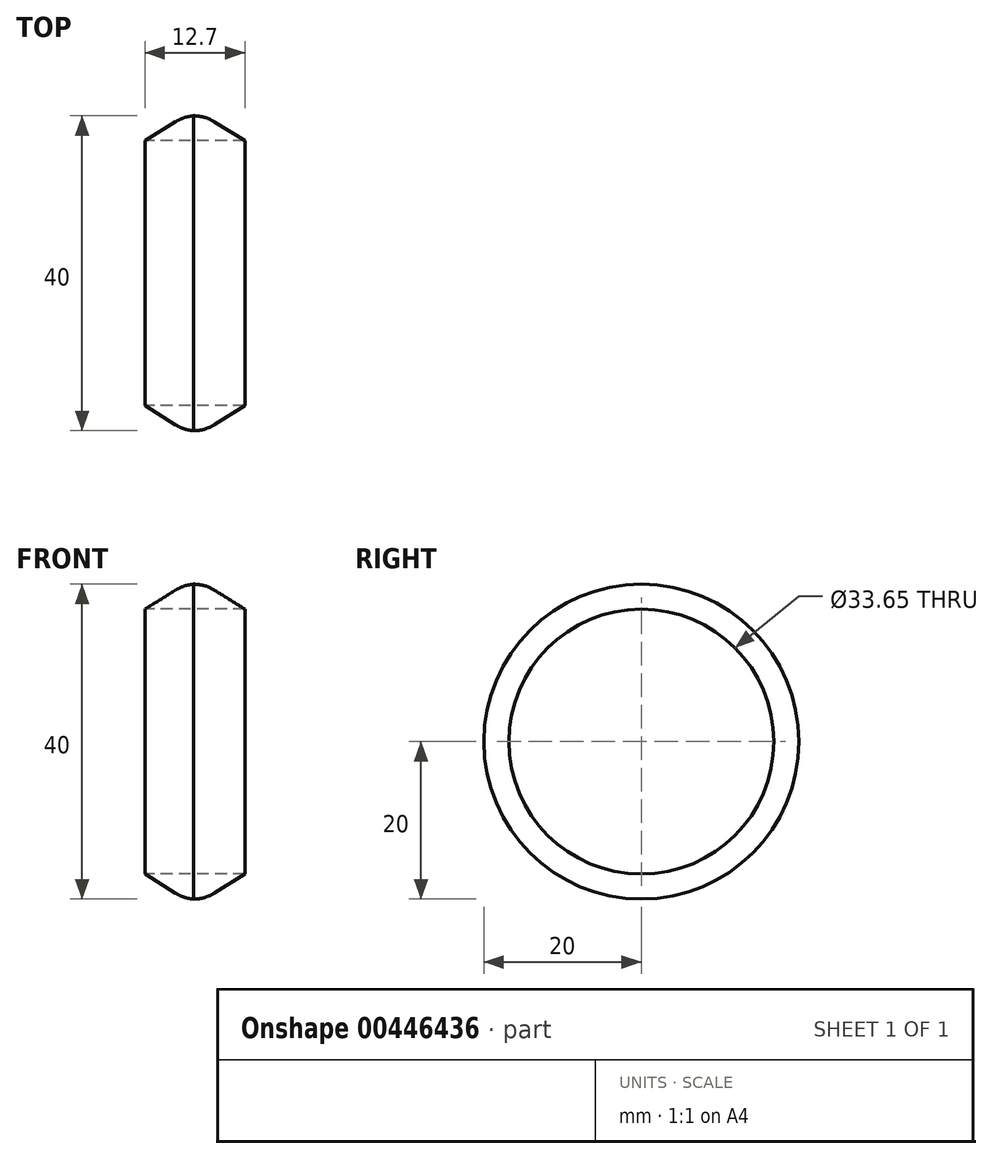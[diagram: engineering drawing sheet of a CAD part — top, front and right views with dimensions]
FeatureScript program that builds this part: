
annotation { "Feature Type Name" : "Feature", "Feature Type Description" : "" }
export const myFeature = defineFeature(function(context is Context, id is Id, definition is map)
    precondition{}
    {
        {
            var Q0;
            Q0=qCreatedBy(makeId("Front.planeOp"),FACE);
            var sketch = newSketch(context, id + "F0", { "sketchPlane" : qUnion([Q0])});
            skLineSegment(sketch, "E0", {"start": v(0, 20) * mm, "end": v(1.27, 20) * mm});
            skLineSegment(sketch, "E1", {"start": v(1.27, 20) * mm, "end": v(6.35, 16.83) * mm});
            skLineSegment(sketch, "E2", {"start": v(6.35, 16.83) * mm, "end": v(1.27, 13.65) * mm});
            skLineSegment(sketch, "E3", {"start": v(1.27, 13.65) * mm, "end": v(0, 13.65) * mm});
            skLineSegment(sketch, "E4.MirrorCS", {"start": v(-6.35, 16.83) * mm, "end": v(-1.27, 13.65) * mm});
            skLineSegment(sketch, "E5.MirrorCS", {"start": v(0, 20) * mm, "end": v(-1.27, 20) * mm});
            skLineSegment(sketch, "E6.MirrorCS", {"start": v(-1.27, 20) * mm, "end": v(-6.35, 16.83) * mm});
            skLineSegment(sketch, "E7.MirrorCS", {"start": v(-1.27, 13.65) * mm, "end": v(0, 13.65) * mm});
            skLineSegment(sketch, "E8", {"start": v(-6.35, 16.83) * mm, "end": v(6.35, 16.83) * mm});
            skSolve(sketch);
        }
        {
            var Q0;
            Q0=qCreatedBy(makeId("Front.planeOp"),FACE);
            var sketch = newSketch(context, id + "F1", { "sketchPlane" : qUnion([Q0])});
            skLineSegment(sketch, "E9", {"start": v(-40.2, 0) * mm, "end": v(49.22, 0) * mm});
            skSolve(sketch);
        }
        {
            var Q0;
            Q0=makeQuery(id+"F0.imprint","IMPRINT",FACE,{"disambiguationData":[TD([[makeQuery(id+"F0.imprint","IMPRINT",EDGE,{"derivedFrom":sQuery(id+"F0.wireOp",EDGE,"E0")}),-1.0]])]});
            var Q1;
            Q1=sQuery(id+"F1.wireOp",EDGE,"E9");
            revolve(context, id + "F2", {"entities" : qUnion([Q0]), "axis" : qUnion([Q1]), "revolveType" : RevolveType.FULL});
        }
        {
            var Q0;
            Q0=makeQuery(id+"F2.opRevolve","SWEPT_EDGE",EDGE,{"disambiguationData":[OSD([sQuery(id+"F0.wireOp",EDGE,"E0"),sQuery(id+"F0.wireOp",EDGE,"E1")])]});
            fillet(context, id + "F3", {"entities" : qUnion([Q0]), "radius" : 5.08 * mm, "tangentPropagation" : true, "allowEdgeOverflow" : false});
        }
        {
            var Q0;
            Q0=makeQuery(id+"F2.opRevolve","SWEPT_EDGE",EDGE,{"disambiguationData":[OSD([sQuery(id+"F0.wireOp",EDGE,"E5.MirrorCS"),sQuery(id+"F0.wireOp",EDGE,"E6.MirrorCS")])]});
            fillet(context, id + "F4", {"entities" : qUnion([Q0]), "radius" : 5.08 * mm, "tangentPropagation" : true, "allowEdgeOverflow" : false});
        }
    });
